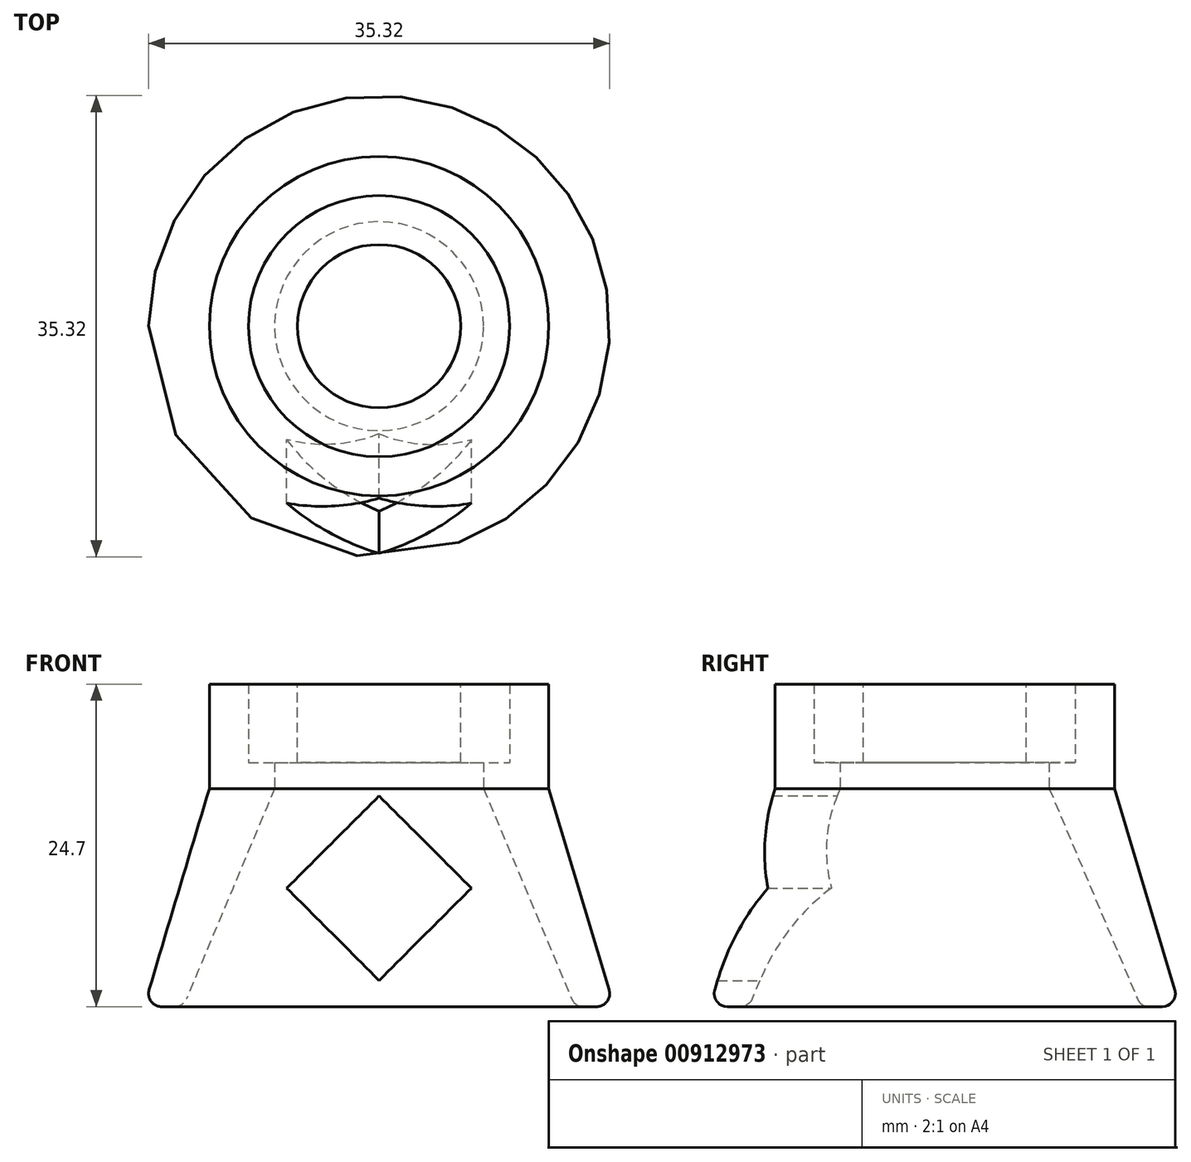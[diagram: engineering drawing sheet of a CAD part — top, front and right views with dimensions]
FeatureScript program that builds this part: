
annotation { "Feature Type Name" : "Feature", "Feature Type Description" : "" }
export const myFeature = defineFeature(function(context is Context, id is Id, definition is map)
    precondition{}
    {
        {
            assignVariable(context, id + "F0", {"name" : "bearing_thickness", "anyValue" : 6});
        }
        {
            assignVariable(context, id + "F1", {"name" : "tool_length", "anyValue" : 24});
        }
        {
            var Q0;
            Q0=qCreatedBy(makeId("Front.planeOp"),FACE);
            var sketch = newSketch(context, id + "F2", { "sketchPlane" : qUnion([Q0])});
            skLineSegment(sketch, "E0.bottom", {"start": v(-10, 6) * mm, "end": v(-3, 6) * mm});
            skLineSegment(sketch, "E0.top", {"start": v(-10, 0) * mm, "end": v(-3, 0) * mm});
            skLineSegment(sketch, "E0.left", {"start": v(-10, 6) * mm, "end": v(-10, 0) * mm});
            skLineSegment(sketch, "E0.right", {"start": v(-3, 6) * mm, "end": v(-3, 0) * mm});
            skLineSegment(sketch, "E1", {"start": v(0, 0) * mm, "end": v(0, 15.14) * mm, "construction": true});
            skSolve(sketch);
        }
        {
            var Q0;
            Q0=makeQuery(id+"F2.imprint","IMPRINT",FACE,{"disambiguationData":[TD([[makeQuery(id+"F2.imprint","IMPRINT",EDGE,{"derivedFrom":sQuery(id+"F2.wireOp",EDGE,"E0.bottom")}),-1.0]])]});
            var Q1;
            Q1=sQuery(id+"F2.wireOp",EDGE,"E1");
            revolve(context, id + "F3", {"surfaceOperationType" : NewSurfaceOperationType.NEW, "entities" : qUnion([Q0]), "axis" : qUnion([Q1]), "revolveType" : RevolveType.FULL});
        }
        {
            var Q0;
            Q0=qCreatedBy(makeId("Front.planeOp"),FACE);
            var sketch = newSketch(context, id + "F4", { "sketchPlane" : qUnion([Q0])});
            skLineSegment(sketch, "E2.top", {"start": v(-10, 0) * mm, "end": v(-8, 0) * mm});
            skLineSegment(sketch, "E2.left", {"start": v(-10, 6) * mm, "end": v(-10, 0) * mm});
            skLineSegment(sketch, "E3", {"start": v(0, 0) * mm, "end": v(0, 15.14) * mm, "construction": true});
            skLineSegment(sketch, "E4", {"start": v(-10, 6) * mm, "end": v(-13, 6) * mm});
            skPoint(sketch, "E5", {"position": v(-8, 0) * mm});
            skLineSegment(sketch, "E6", {"start": v(-8, 0) * mm, "end": v(-8, -2) * mm});
            skLineSegment(sketch, "E7", {"start": v(-14.74, -18.09) * mm, "end": v(-8, -2) * mm});
            skLineSegment(sketch, "E8", {"start": v(-13, 6) * mm, "end": v(-13, -2) * mm});
            skLineSegment(sketch, "E9", {"start": v(-15.67, -18.7) * mm, "end": v(-16.66, -18.7) * mm});
            skLineSegment(sketch, "E10", {"start": v(-17.61, -17.41) * mm, "end": v(-13, -2) * mm});
            skPoint(sketch, "E11.visualSharp", {"position": v(-18, -18.7) * mm});
            skArc(sketch, "E11.filletArc", {"start": v(-17.61, -17.41) * mm, "mid": v(-17.46, -18.3) * mm, "end": v(-16.66, -18.7) * mm});
            skPoint(sketch, "E12.visualSharp", {"position": v(-15, -18.7) * mm});
            skArc(sketch, "E12.filletArc", {"start": v(-15.67, -18.7) * mm, "mid": v(-15.11, -18.53) * mm, "end": v(-14.74, -18.09) * mm});
            skSolve(sketch);
        }
        {
            var Q0;
            Q0 = qSketchRegion(id + "F4", true);
            var Q1;
            Q1=sQuery(id+"F4.wireOp",EDGE,"E3");
            revolve(context, id + "F5", {"surfaceOperationType" : NewSurfaceOperationType.NEW, "entities" : qUnion([Q0]), "axis" : qUnion([Q1]), "revolveType" : RevolveType.FULL});
        }
        {
            var Q0;
            Q0=makeQuery(id+"F3.opRevolve","SWEPT_FACE",FACE,{"disambiguationData":[OSD([sQuery(id+"F2.wireOp",EDGE,"E0.bottom")])]});
            var sketch = newSketch(context, id + "F6", { "sketchPlane" : qUnion([Q0])});
            skCircle(sketch, "E13", {"center": v(0, 0) * mm, "radius": 6.25 * mm});
            skSolve(sketch);
        }
        {
            var Q0;
            Q0 = qSketchRegion(id + "F6", true);
            extrude(context, id + "F7", {"entities" : qUnion([Q0]), "operationType" : NewBodyOperationType.REMOVE, "oppositeDirection" : true, "depth" : (getVariable(context, 'bearing_thickness') + getVariable(context, 'tool_length')) * mm, "offsetDistance" : 25 * mm});
        }
        {
            var Q0;
            Q0=qCreatedBy(makeId("Front.planeOp"),FACE);
            var sketch = newSketch(context, id + "F8", { "sketchPlane" : qUnion([Q0])});
            skLineSegment(sketch, "E14.bottom", {"start": v(0, -2.56) * mm, "end": v(7.07, -9.63) * mm});
            skLineSegment(sketch, "E14.top", {"start": v(-7.07, -9.63) * mm, "end": v(0, -16.7) * mm});
            skLineSegment(sketch, "E14.left", {"start": v(0, -2.56) * mm, "end": v(-7.07, -9.63) * mm});
            skLineSegment(sketch, "E14.right", {"start": v(7.07, -9.63) * mm, "end": v(0, -16.7) * mm});
            skSolve(sketch);
        }
        {
            var Q0;
            Q0 = qSketchRegion(id + "F8", true);
            extrude(context, id + "F9", {"entities" : qUnion([Q0]), "operationType" : NewBodyOperationType.REMOVE, "depth" : 80 * mm, "offsetDistance" : 25 * mm});
        }
    });
